# Revit family: EV-HMI7WF HMI Control Panel
name_source: partatom
category: Generic Models
units: mm (PartAtom-declared; Revit-internal decimal feet)

## family parameters
Always vertical = No
Can host rebar = No
Cut with Voids When Loaded = No
OmniClass Number = 23.40.00.00
OmniClass Title = Equipment and Furnishings
Part Type = Normal
Room Calculation Point = No
Round Connector Dimension = Use Diameter
Shared = No
Work Plane-Based = Yes

## types (1)
- Controls
    BIMObject Category_2 = Controllers
    BIMobject category = Electrical
    Colour = White Gloss/ Matt Black
    Connection cable = 3 Core FP200 Data Connection
    Control Connections - Material Secondary = White Plastic Connections
    Cost = 0 $
    Current consumption = 0.5A
    Default Elevation = 1200 mm
    Depth = 96 mm
    Description = 7" TFT portrait touch display, LED backlit, 65536 colours, 20,000 hours MTBF. 8 Function keys for navigating & override command.
    Design country = UK
    Edition number = 1
    Features = Can be flush or surface mounted
    Finish = ABS White Gloss
    Green Tag = Smoke Control Banner
    Height = 296 mm
    IFC Classification = Controller
    IP rating = IP42
    Keynote = Wall Mounted
    Manufacturer = Easivent
    Manufacturer URL = http://easivent.co.uk
    Manufacturer country = UK
    Manufacturer name = Easivent
    Model = HMI7WF White, HMI7BF Black
    NBS Reference Code = 16-16-15
    NBS Reference Description = Control Panels
    Name of the object = HMI User Interface Smoke Control Panel
    Nominal height = 296
    Nominal width = 240
    Notes = Please note this product may be amended without prior notification
    Product family = Interfaces
    Product group = Controls
    Screen Material = Glass
    SerialNumber = 0
    Size = 240x96x296mm (W x D x H)
    TagNumber = 0
    Technical description = The HMI is the user interface panel to the smoke shaft system providing configuration override control & monitoring functions via a colour touch screen with function keys. Password protection prevents unauthorised operation in normal conditions and is automatically removed in the event of a fire. Dynamic function keys provide easy navigation and quick access to firemans override control even when wearing gloves.
    To be ordered separately = All other system components
    Type Comments = CE marked to low voltage & EMC directives
    Uniclass 2.0 Code = Pr_16_16_15
    Uniclass 2.0 Description = Control Panels
    Uniclass 2015 Code = Pr_75_50_18
    Uniclass 2015 Name = Controllers & Control Panels
    Voltage = 230V AC
    WarrantyDuration = 12
    WarrantyStartDate = From items dispatch
    Weight = 2
    Weight Net (Kg) = 0
    White Label - Material = White Plastic
    Width = 240

## geometry (parser evidence)
native form markers: Blend x2, Sweep x9
no freeform markers — native parametric forms only
